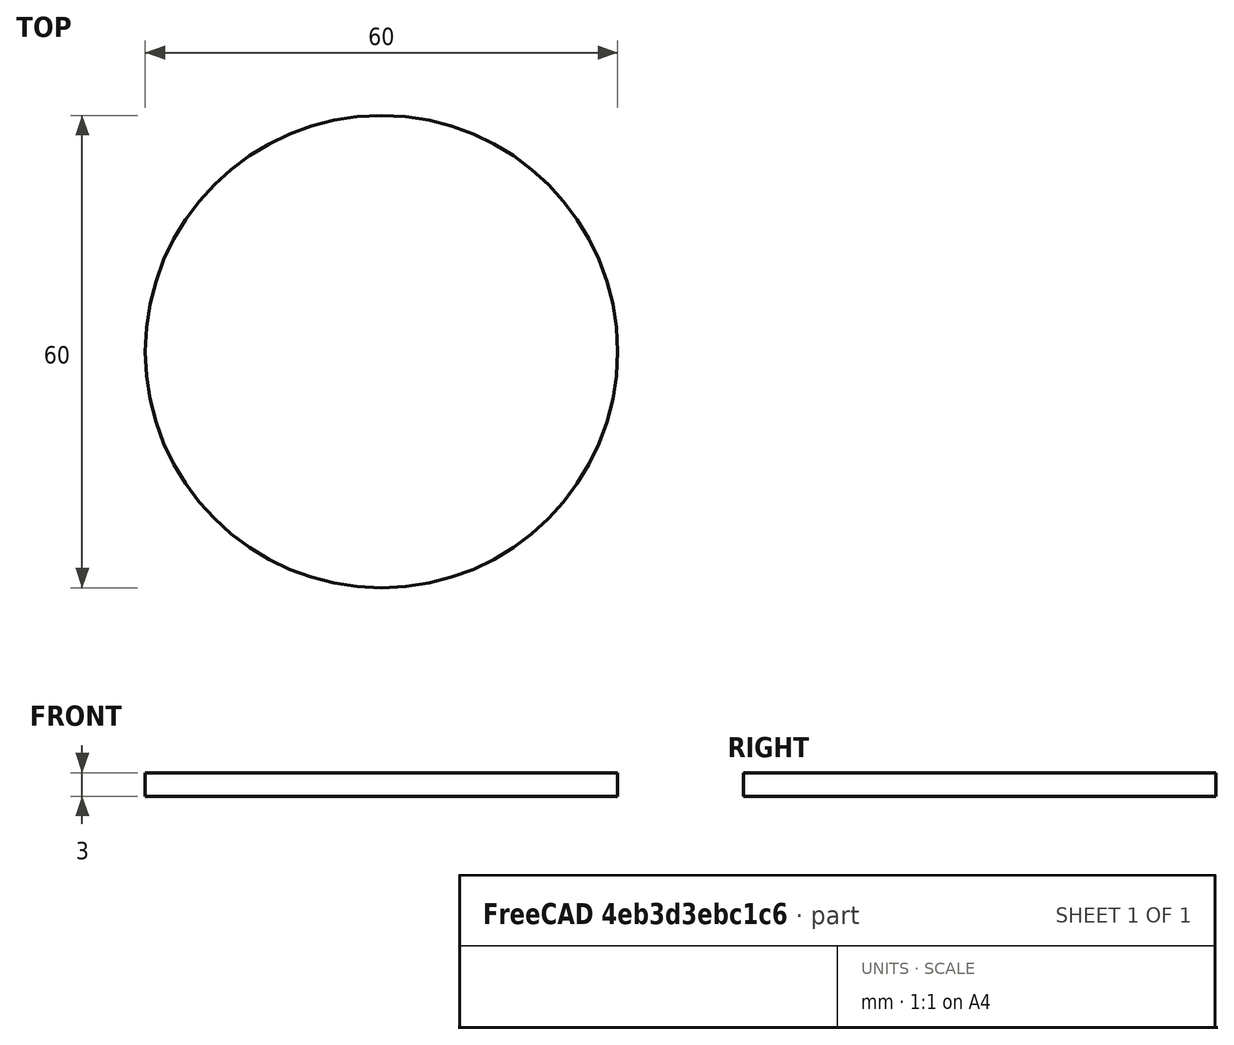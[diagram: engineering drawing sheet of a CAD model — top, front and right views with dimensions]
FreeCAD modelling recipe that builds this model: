
FCSTD DOCUMENT  (FreeCAD 0.18R16117 (Git))
Label: sASasASasASa
License: All rights reserved
LicenseURL: http://en.wikipedia.org/wiki/All_rights_reserved
objects: Sketcher::SketchObject×1, PartDesign::Pad×1, PartDesign::Body×1
note: 4 computed .brp shape members not serialized (recipe doc carries the construction recipe); baked Part::Feature solids carry a one-line shape summary decoded from their .brp

FEATURE [Sketcher::SketchObject] Sketch
  MapMode = 5
  Support = -> [XY_Plane]
  sketch-geometry (5):
    g0: LineSegment [constr] StartX=-50 StartY=50 StartZ=0 EndX=50 EndY=50 EndZ=0
    g1: LineSegment [constr] StartX=50 StartY=50 StartZ=0 EndX=50 EndY=-50 EndZ=0
    g2: LineSegment [constr] StartX=50 StartY=-50 StartZ=0 EndX=-50 EndY=-50 EndZ=0
    g3: LineSegment [constr] StartX=-50 StartY=-50 StartZ=0 EndX=-50 EndY=50 EndZ=0
    g4: Circle CenterX=0 CenterY=0 CenterZ=0 NormalX=0 NormalY=0 NormalZ=1 AngleXU=0 Radius=30
  constraints (11):
    c: Coincident(g0,g1)
    c: Coincident(g1,g2)
    c: Coincident(g2,g3)
    c: Coincident(g3,g0)
    c: Horizontal(g2)
    c: Vertical(g3)
    c: DistanceX(g0,g0) = 100
    c: DistanceY(g1,g1) = 100
    c: Symmetric(g1,g0,g-1)
    c: Symmetric(g0,g0,g-2)
    c: Radius(g4) = 30
FEATURE [PartDesign::Pad] Pad
  Length = 3
  Length2 = 100
  Profile = -> Sketch
  Type = 0
FEATURE [PartDesign::Body] Body
  Group = -> [Sketch,Pad]
  Origin = -> Origin
  Tip = -> Pad
